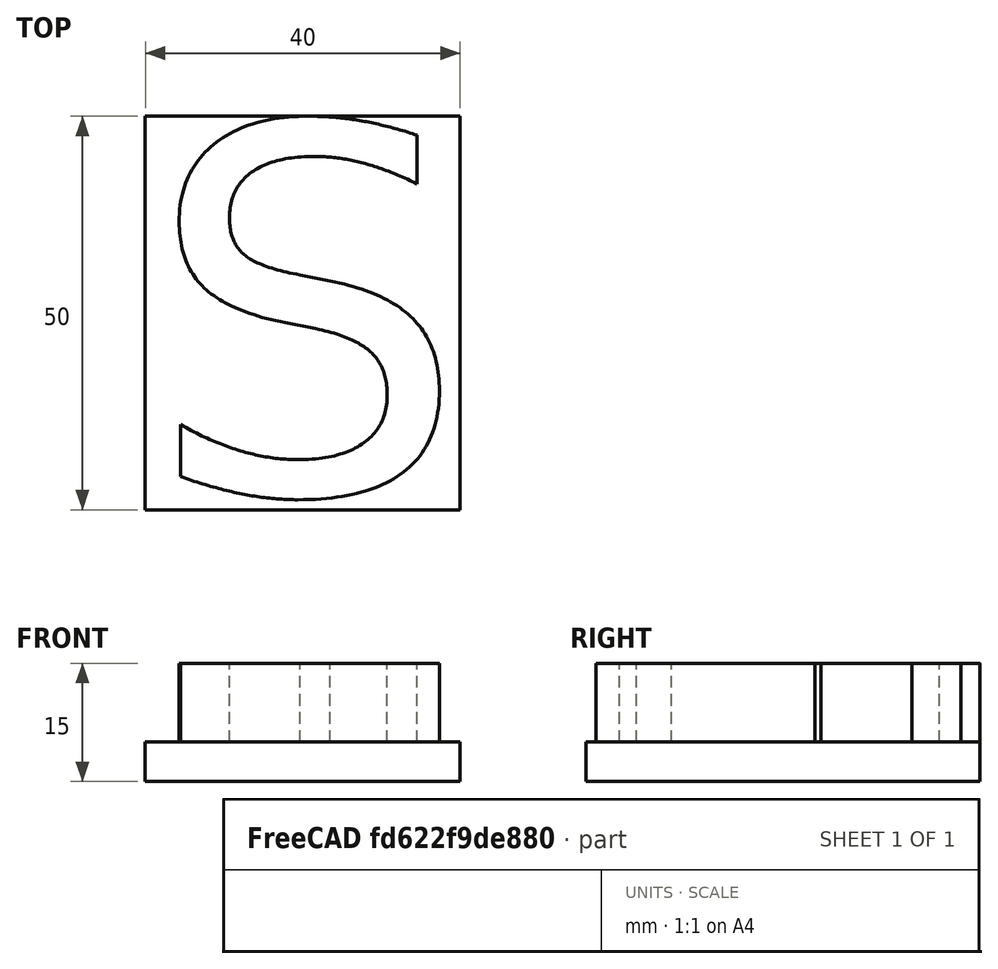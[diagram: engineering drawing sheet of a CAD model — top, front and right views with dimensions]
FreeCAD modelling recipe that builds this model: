
FCSTD DOCUMENT  (FreeCAD 0.21RUnknown)
Label: s-sketch
License: All rights reserved
LicenseURL: https://en.wikipedia.org/wiki/All_rights_reserved
objects: Part::Part2DObjectPython×2, Sketcher::SketchObject×2, Part::Extrusion×1, PartDesign::Pad×1, PartDesign::Body×1
note: 8 computed .brp shape members not serialized (recipe doc carries the construction recipe); baked Part::Feature solids carry a one-line shape summary decoded from their .brp

FEATURE [Part::Part2DObjectPython] Rectangle  # Draft 2D object (typed FeaturePython)
  Area = 2000
  ChamferSize = 0
  Columns = 1
  FilletRadius = 0
  Height = 50
  Length = 40
  MakeFace = true
  Placement = pos=(-0.0534207,-0.213677,0) rot=(0,0,1;0rad)
  Rows = 1
FEATURE [Part::Extrusion] Extrusion
  Base = -> Rectangle
  Dir = (0,0,5)
  DirMode = 0
  FaceMakerClass = Part::FaceMakerBullseye
  LengthFwd = 0
  LengthRev = 0
  Solid = true
  Symmetric = false
FEATURE [Part::Part2DObjectPython] ShapeString  # Draft 2D object (typed FeaturePython)
  FontFile = /nix/var/nix/profiles/system/sw/share/X11/fonts/DejaVuSans.ttf
  MakeFace = true
  Placement = pos=(0,2,5) rot=(0,0,1;0rad)
  Size = 50
  String = S
  Tracking = 0
FEATURE [Sketcher::SketchObject] Sketch
  FullyConstrained = false
  Placement = pos=(0,0,5) rot=(0,0,1;0rad)
  sketch-geometry (28):
    g0: LineSegment StartX=34.4799 StartY=47.3691 StartZ=0 EndX=34.4799 EndY=41.1946 EndZ=0
    g1: BSplineCurve PolesCount=3 KnotsCount=2 Degree=2 IsPeriodic=0
    g2: BSplineCurve PolesCount=3 KnotsCount=2 Degree=2 IsPeriodic=0
    g3: BSplineCurve PolesCount=3 KnotsCount=2 Degree=2 IsPeriodic=0
    g4: BSplineCurve PolesCount=3 KnotsCount=2 Degree=2 IsPeriodic=0
    g5: BSplineCurve PolesCount=3 KnotsCount=2 Degree=2 IsPeriodic=0
    g6: BSplineCurve PolesCount=3 KnotsCount=2 Degree=2 IsPeriodic=0
    g7: LineSegment StartX=21.5814 StartY=22.7949 StartZ=0 EndX=17.7118 EndY=23.5499 EndZ=0
    g8: BSplineCurve PolesCount=3 KnotsCount=2 Degree=2 IsPeriodic=0
    g9: BSplineCurve PolesCount=3 KnotsCount=2 Degree=2 IsPeriodic=0
    g10: BSplineCurve PolesCount=3 KnotsCount=2 Degree=2 IsPeriodic=0
    g11: BSplineCurve PolesCount=3 KnotsCount=2 Degree=2 IsPeriodic=0
    g12: BSplineCurve PolesCount=3 KnotsCount=2 Degree=2 IsPeriodic=0
    g13: BSplineCurve PolesCount=3 KnotsCount=2 Degree=2 IsPeriodic=0
    g14: LineSegment StartX=4.43582 StartY=4.01342 StartZ=0 EndX=4.43582 EndY=10.5906 EndZ=0
    g15: BSplineCurve PolesCount=3 KnotsCount=2 Degree=2 IsPeriodic=0
    g16: BSplineCurve PolesCount=3 KnotsCount=2 Degree=2 IsPeriodic=0
    g17: BSplineCurve PolesCount=3 KnotsCount=2 Degree=2 IsPeriodic=0
    g18: BSplineCurve PolesCount=3 KnotsCount=2 Degree=2 IsPeriodic=0
    g19: BSplineCurve PolesCount=3 KnotsCount=2 Degree=2 IsPeriodic=0
    g20: BSplineCurve PolesCount=3 KnotsCount=2 Degree=2 IsPeriodic=0
    g21: LineSegment StartX=19.5994 StartY=29.6195 StartZ=0 EndX=23.4375 EndY=28.8331 EndZ=0
    g22: BSplineCurve PolesCount=3 KnotsCount=2 Degree=2 IsPeriodic=0
    g23: BSplineCurve PolesCount=3 KnotsCount=2 Degree=2 IsPeriodic=0
    g24: BSplineCurve PolesCount=3 KnotsCount=2 Degree=2 IsPeriodic=0
    g25: BSplineCurve PolesCount=3 KnotsCount=2 Degree=2 IsPeriodic=0
    g26: BSplineCurve PolesCount=3 KnotsCount=2 Degree=2 IsPeriodic=0
    g27: BSplineCurve PolesCount=3 KnotsCount=2 Degree=2 IsPeriodic=0
  constraints (30):
    c: Vertical(g0)
    c: Coincident(g0,g1)
    c: Coincident(g1,g2)
    c: Coincident(g2,g3)
    c: Coincident(g3,g4)
    c: Coincident(g4,g5)
    c: Coincident(g5,g6)
    c: Coincident(g6,g7)
    c: Coincident(g7,g8)
    c: Coincident(g8,g9)
    c: Coincident(g9,g10)
    c: Coincident(g10,g11)
    c: Coincident(g11,g12)
    c: Coincident(g12,g13)
    c: Coincident(g13,g14)
    c: Vertical(g14)
    c: Coincident(g14,g15)
    c: Coincident(g15,g16)
    c: Coincident(g16,g17)
    c: Coincident(g17,g18)
    c: Coincident(g18,g19)
    c: Coincident(g19,g20)
    c: Coincident(g20,g21)
    c: Coincident(g21,g22)
    c: Coincident(g22,g23)
    c: Coincident(g23,g24)
    c: Coincident(g24,g25)
    c: Coincident(g25,g26)
    c: Coincident(g26,g27)
    c: Coincident(g27,g0)
FEATURE [Sketcher::SketchObject] Sketch001
  FullyConstrained = true
  MapMode = 5
  Support = -> [XY_Plane]
FEATURE [PartDesign::Pad] Pad
  Direction = (0,0,1)
  Length = 10
  Length2 = 10
  Placement = pos=(0,0,5) rot=(0,0,1;0rad)
  Profile = -> Sketch
  ReferenceAxis = -> Sketch [N_Axis]
  Type = 0
FEATURE [PartDesign::Body] Body
  Group = -> [Sketch001,Sketch,Pad]
  Origin = -> Origin
  Tip = -> Pad
